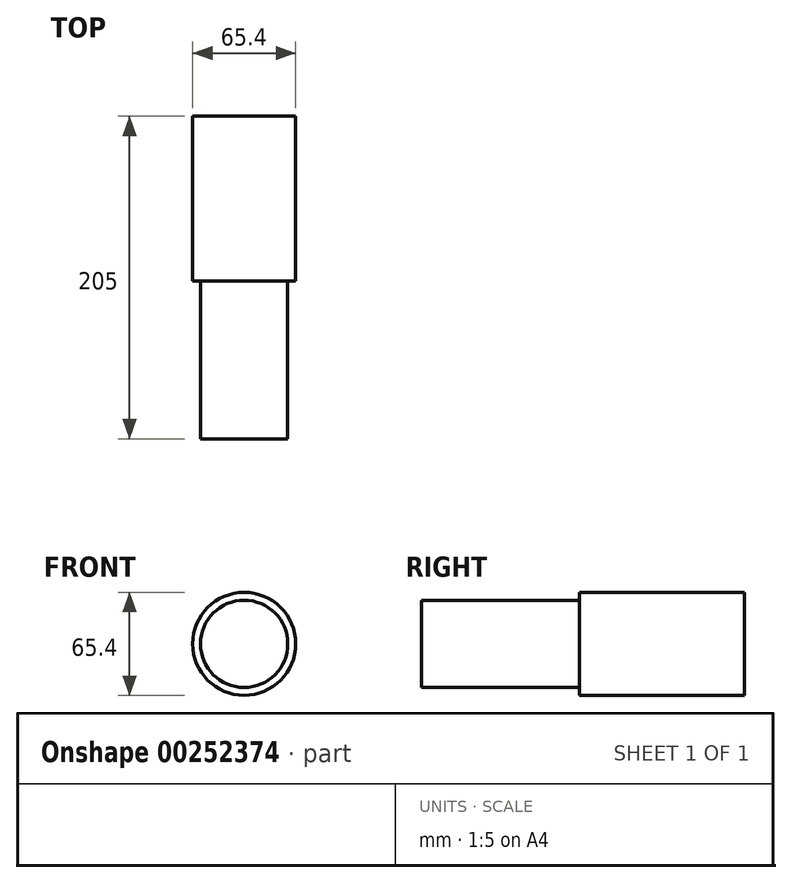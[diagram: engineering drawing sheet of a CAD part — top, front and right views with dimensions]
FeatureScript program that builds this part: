
annotation { "Feature Type Name" : "Feature", "Feature Type Description" : "" }
export const myFeature = defineFeature(function(context is Context, id is Id, definition is map)
    precondition{}
    {
        {
            var Q0;
            Q0=qCreatedBy(makeId("Top.planeOp"),FACE);
            var sketch = newSketch(context, id + "F0", { "sketchPlane" : qUnion([Q0])});
            skLineSegment(sketch, "E0.bottom", {"start": v(32.7, 52.36) * mm, "end": v(-32.7, 52.36) * mm});
            skLineSegment(sketch, "E0.top", {"start": v(32.7, -52.36) * mm, "end": v(-32.7, -52.36) * mm});
            skLineSegment(sketch, "E0.left", {"start": v(32.7, 52.36) * mm, "end": v(32.7, -52.36) * mm});
            skLineSegment(sketch, "E0.right", {"start": v(-32.7, 52.36) * mm, "end": v(-32.7, -52.36) * mm});
            skPoint(sketch, "E0.middle", {"position": v(0, 0) * mm});
            skLineSegment(sketch, "E1", {"start": v(0, 52.36) * mm, "end": v(0, -52.36) * mm});
            skSolve(sketch);
        }
        {
            var Q0;
            {var subQ0=sQuery(id+"F0.wireOp",EDGE,"E0.right");Q0=makeQuery(id+"F0.imprint","IMPRINT",FACE,{"disambiguationData":[TD([[makeQuery(id+"F0.imprint","IMPRINT",EDGE,{"derivedFrom":subQ0}),1.0]])]});}
            var Q1;
            Q1=sQuery(id+"F0.wireOp",EDGE,"E1");
            revolve(context, id + "F1", {"entities" : qUnion([Q0]), "axis" : qUnion([Q1]), "revolveType" : RevolveType.FULL});
        }
        {
            var Q0;
            Q0=makeQuery(id+"F1.opRevolve","SWEPT_FACE",FACE,{"disambiguationData":[OSD([sQuery(id+"F0.wireOp",EDGE,"E0.top")])]});
            shell(context, id + "F2", {"entities" : qUnion([Q0]), "thickness" : 5 * mm});
        }
        {
            var Q0;
            Q0=makeQuery(id+"F2.opShell","OFFSET_FACE",FACE,{"disambiguationData":[OSD([sQuery(id+"F0.wireOp",EDGE,"E0.bottom")])]});
            extrude(context, id + "F3", {"entities" : qUnion([Q0]), "operationType" : NewBodyOperationType.ADD, "depth" : 200 * mm});
        }
    });
